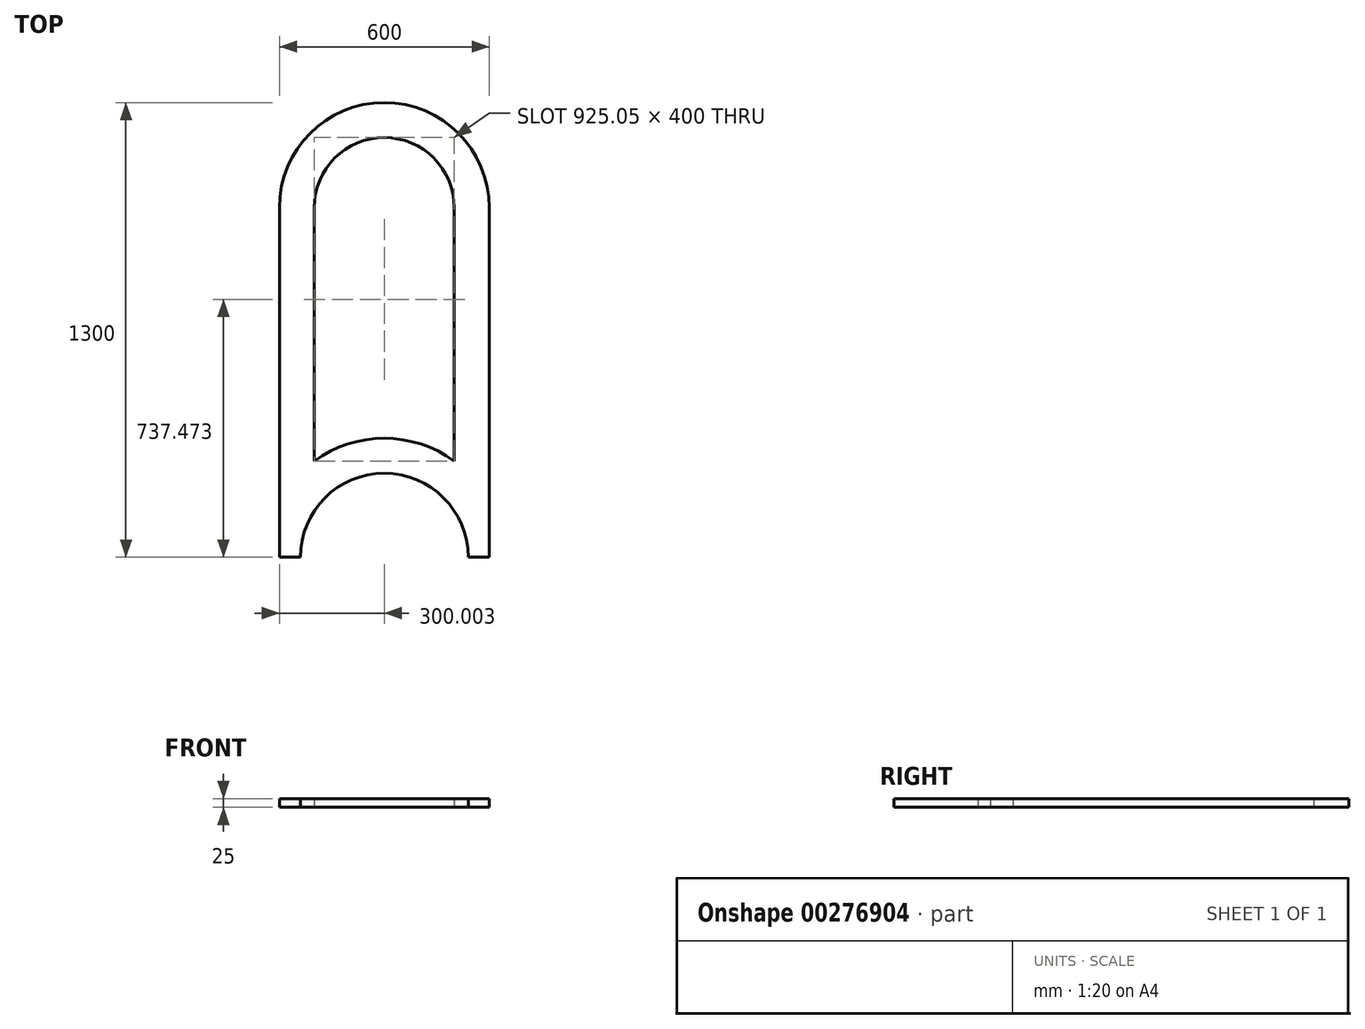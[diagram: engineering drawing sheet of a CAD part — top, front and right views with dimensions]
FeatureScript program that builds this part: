
annotation { "Feature Type Name" : "Feature", "Feature Type Description" : "" }
export const myFeature = defineFeature(function(context is Context, id is Id, definition is map)
    precondition{}
    {
        {
            var Q0;
            Q0=qCreatedBy(makeId("Top.planeOp"),FACE);
            var sketch = newSketch(context, id + "F0", { "sketchPlane" : qUnion([Q0])});
            skLineSegment(sketch, "E0", {"start": v(-48.9, -32.6) * mm, "end": v(11.1, -32.6) * mm});
            skLineSegment(sketch, "E1", {"start": v(551.1, -32.6) * mm, "end": v(551.1, 967.4) * mm});
            skLineSegment(sketch, "E2", {"start": v(551.1, -32.6) * mm, "end": v(491.1, -32.6) * mm});
            skPoint(sketch, "E3", {"position": v(251.1, -32.6) * mm});
            skLineSegment(sketch, "E4.trimOffspring", {"start": v(491.1, -32.6) * mm, "end": v(551.1, -32.6) * mm});
            skArc(sketch, "E5", {"start": v(491.1, -32.6) * mm, "mid": v(251.1, 207.4) * mm, "end": v(11.1, -32.6) * mm});
            skLineSegment(sketch, "E6", {"start": v(-48.9, -32.6) * mm, "end": v(-48.9, 967.4) * mm});
            skArc(sketch, "E7", {"start": v(451.1, 242.35) * mm, "mid": v(251.1, 307.4) * mm, "end": v(51.1, 242.35) * mm});
            skArc(sketch, "E8", {"start": v(451.1, 967.4) * mm, "mid": v(251.1, 1167.4) * mm, "end": v(51.1, 967.4) * mm});
            skArc(sketch, "E9", {"start": v(551.1, 967.4) * mm, "mid": v(251.1, 1267.4) * mm, "end": v(-48.9, 967.4) * mm});
            skLineSegment(sketch, "E10", {"start": v(451.1, 967.4) * mm, "end": v(451.1, 242.35) * mm});
            skLineSegment(sketch, "E11", {"start": v(51.1, 967.4) * mm, "end": v(51.1, 242.35) * mm});
            skLineSegment(sketch, "E12.trimOffspring", {"start": v(11.1, -32.6) * mm, "end": v(-48.9, -32.6) * mm});
            skSolve(sketch);
        }
        {
            var Q0;
            Q0 = qSketchRegion(id + "F0", true);
            extrude(context, id + "F1", {"entities" : qUnion([Q0]), "depth" : 25 * mm});
        }
    });
